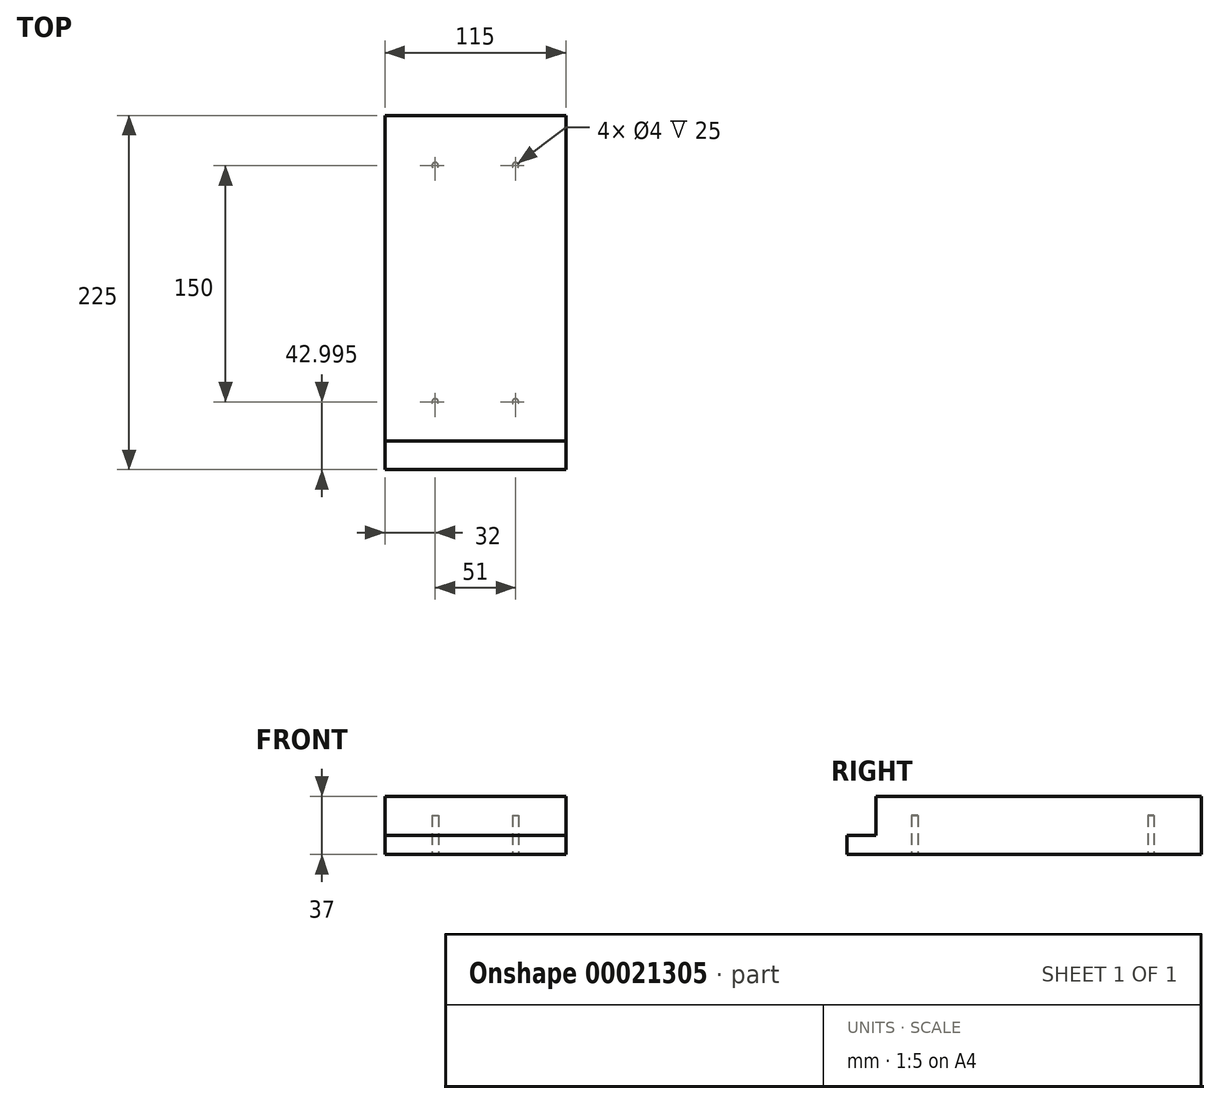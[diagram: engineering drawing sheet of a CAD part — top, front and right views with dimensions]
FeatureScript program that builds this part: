
annotation { "Feature Type Name" : "Feature", "Feature Type Description" : "" }
export const myFeature = defineFeature(function(context is Context, id is Id, definition is map)
    precondition{}
    {
        {
            var Q0;
            Q0=qCreatedBy(makeId("Top.planeOp"),FACE);
            var sketch = newSketch(context, id + "F0", { "sketchPlane" : qUnion([Q0])});
            skLineSegment(sketch, "E0.bottom", {"start": v(-64.59, 138.4) * mm, "end": v(50.41, 138.4) * mm});
            skLineSegment(sketch, "E0.top", {"start": v(-64.59, -86.6) * mm, "end": v(50.41, -86.6) * mm});
            skLineSegment(sketch, "E0.left", {"start": v(-64.59, 138.4) * mm, "end": v(-64.59, -86.6) * mm});
            skLineSegment(sketch, "E0.right", {"start": v(50.41, 138.4) * mm, "end": v(50.41, -86.6) * mm});
            skSolve(sketch);
        }
        {
            var Q0;
            Q0 = qSketchRegion(id + "F0", true);
            extrude(context, id + "F1", {"entities" : qUnion([Q0]), "depth" : 37 * mm});
        }
        {
            var Q0;
            Q0=makeQuery(id+"F1.opExtrude","CAP_FACE",FACE,{"disambiguationData":[OSD([sQuery(id+"F0.wireOp",EDGE,"E0.bottom"),sQuery(id+"F0.wireOp",EDGE,"E0.top"),sQuery(id+"F0.wireOp",EDGE,"E0.left"),sQuery(id+"F0.wireOp",EDGE,"E0.right")])],"isStart":true});
            var sketch = newSketch(context, id + "F2", { "sketchPlane" : qUnion([Q0])});
            skLineSegment(sketch, "E1.bottom", {"start": v(18.41, -106.4) * mm, "end": v(-32.59, -106.4) * mm, "construction": true});
            skLineSegment(sketch, "E1.top", {"start": v(18.41, 43.6) * mm, "end": v(-32.59, 43.6) * mm, "construction": true});
            skLineSegment(sketch, "E1.left", {"start": v(18.41, -106.4) * mm, "end": v(18.41, 43.6) * mm, "construction": true});
            skLineSegment(sketch, "E1.right", {"start": v(-32.59, -106.4) * mm, "end": v(-32.59, 43.6) * mm, "construction": true});
            skCircle(sketch, "E2", {"center": v(-32.59, -106.4) * mm, "radius": 2 * mm});
            skCircle(sketch, "E3", {"center": v(18.41, -106.4) * mm, "radius": 2 * mm});
            skCircle(sketch, "E4", {"center": v(18.41, 43.6) * mm, "radius": 2 * mm});
            skCircle(sketch, "E5", {"center": v(-32.59, 43.6) * mm, "radius": 2 * mm});
            skSolve(sketch);
        }
        {
            var Q0;
            Q0 = qSketchRegion(id + "F2", true);
            extrude(context, id + "F3", {"entities" : qUnion([Q0]), "operationType" : NewBodyOperationType.REMOVE, "oppositeDirection" : true, "depth" : 25 * mm});
        }
        {
            var Q0;
            Q0=makeQuery(id+"F1.opExtrude","CAP_FACE",FACE,{"disambiguationData":[OSD([sQuery(id+"F0.wireOp",EDGE,"E0.bottom"),sQuery(id+"F0.wireOp",EDGE,"E0.top"),sQuery(id+"F0.wireOp",EDGE,"E0.left"),sQuery(id+"F0.wireOp",EDGE,"E0.right")])],"isStart":false});
            var sketch = newSketch(context, id + "F4", { "sketchPlane" : qUnion([Q0])});
            skLineSegment(sketch, "E6.bottom", {"start": v(-64.59, -86.6) * mm, "end": v(50.41, -86.6) * mm});
            skLineSegment(sketch, "E6.top", {"start": v(-64.59, -68.4) * mm, "end": v(50.41, -68.4) * mm});
            skLineSegment(sketch, "E6.left", {"start": v(-64.59, -86.6) * mm, "end": v(-64.59, -68.4) * mm});
            skLineSegment(sketch, "E6.right", {"start": v(50.41, -86.6) * mm, "end": v(50.41, -68.4) * mm});
            skSolve(sketch);
        }
        {
            var Q0;
            Q0 = qSketchRegion(id + "F4", true);
            extrude(context, id + "F5", {"entities" : qUnion([Q0]), "operationType" : NewBodyOperationType.REMOVE, "oppositeDirection" : true, "depth" : 25 * mm});
        }
    });
